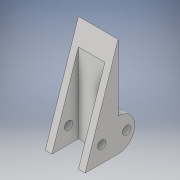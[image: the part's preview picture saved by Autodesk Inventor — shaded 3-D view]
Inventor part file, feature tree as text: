
AUTODESK INVENTOR PART (.ipt)
format: ipt  version: 2019 (Build 230136000, 136)  size: 155,648 bytes
history: native  units: in
note: dims shown in document units (in); Inventor stores cm internally (conversion verified against a paired STEP export)
features: extrude x7, sketch x7
ambient origin geometry x8: Origin, YZ Plane, XZ Plane, XY Plane, X Axis, Y Axis, Z Axis, Center Point
bodies: Body1 (feature_tree)
feature tree (14):
  extrude  "Extrusion2"  Depth=1.5in
  extrude  "Extrusion6"  Depth=0.1in
  extrude  "Extrusion7"  Depth=0.1in
  extrude  "Extrusion8"  Depth=0.4in TaperAngle=0.0deg
  extrude  "Extrusion9"  Depth=0.25in
  extrude  "Extrusion10"  Depth=0.125in
  extrude  "Extrusion11"  Depth=0.25in
  sketch  "Sketch1"  dims[d4=0.6in d5=1.5in]
  sketch  "Sketch8"  dims[d6=0.5in d7=0.0in d22=0.1in]
  sketch  "Sketch9"  dims[d23=0.1in d24=0.1in]
  sketch  "Sketch10"  dims[d25=0.4in d26=0.0in d27=2.0in d28=0.0in]
  sketch  "Sketch11"  dims[d29=0.1in d30=0.0in d31=0.25in]
  sketch  "Sketch12"  dims[d33=0.125in d34=0.0in d35=0.125in]
  sketch  "Sketch13"  dims[d36=0.125in d37=0.0in d38=0.25in d39=0.125in d40=2.0in d41=0.0in]
